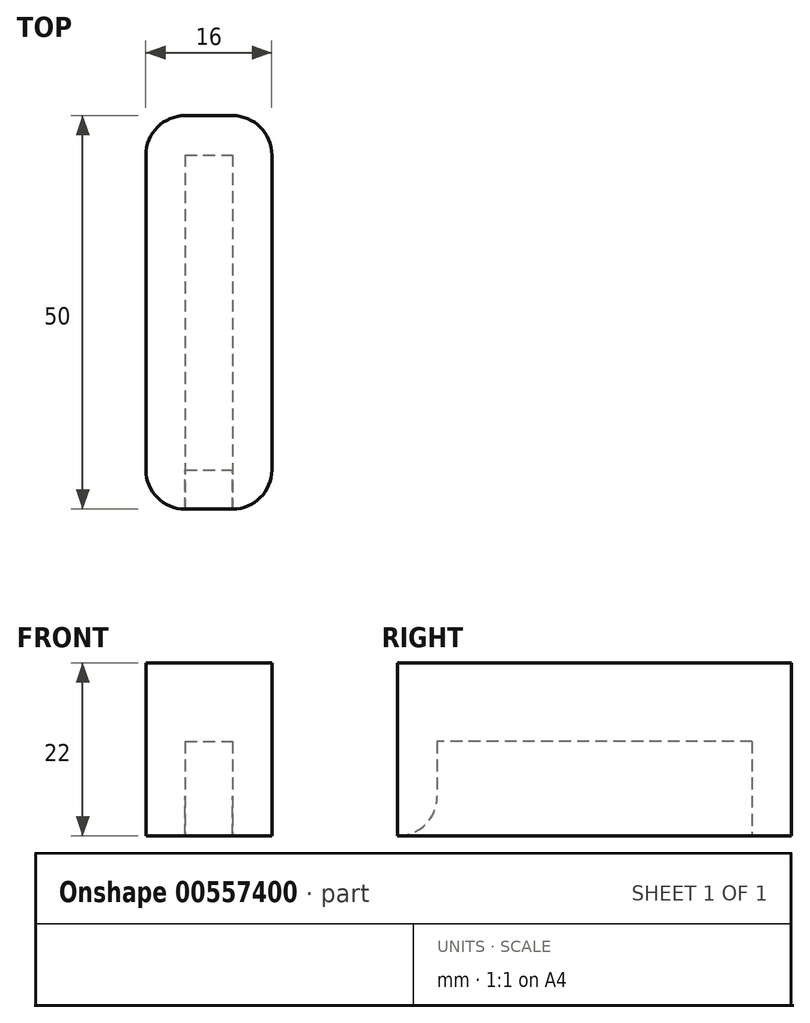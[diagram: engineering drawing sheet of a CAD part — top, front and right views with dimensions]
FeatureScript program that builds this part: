
annotation { "Feature Type Name" : "Feature", "Feature Type Description" : "" }
export const myFeature = defineFeature(function(context is Context, id is Id, definition is map)
    precondition{}
    {
        {
            var Q0;
            Q0=qCreatedBy(makeId("Top.planeOp"),FACE);
            var sketch = newSketch(context, id + "F0", { "sketchPlane" : qUnion([Q0])});
            skLineSegment(sketch, "E0.bottom", {"start": v(-26.05, 14.24) * mm, "end": v(-20.05, 14.24) * mm});
            skLineSegment(sketch, "E0.top", {"start": v(-26.05, -25.76) * mm, "end": v(-20.05, -25.76) * mm});
            skLineSegment(sketch, "E0.left", {"start": v(-26.05, 14.24) * mm, "end": v(-26.05, -25.76) * mm});
            skLineSegment(sketch, "E0.right", {"start": v(-20.05, 14.24) * mm, "end": v(-20.05, -25.76) * mm});
            skLineSegment(sketch, "E1.bottom", {"start": v(-15.05, -30.76) * mm, "end": v(-31.05, -30.76) * mm});
            skLineSegment(sketch, "E1.top", {"start": v(-15.05, 19.24) * mm, "end": v(-31.05, 19.24) * mm});
            skLineSegment(sketch, "E1.left", {"start": v(-15.05, -30.76) * mm, "end": v(-15.05, 19.24) * mm});
            skLineSegment(sketch, "E1.right", {"start": v(-31.05, -30.76) * mm, "end": v(-31.05, 19.24) * mm});
            skSolve(sketch);
        }
        {
            var Q0;
            Q0 = qSketchRegion(id + "F0", true);
            extrude(context, id + "F1", {"entities" : qUnion([Q0]), "depth" : 12 * mm, "offsetDistance" : 25 * mm});
        }
        {
            var Q0;
            Q0=makeQuery(id+"F1.opExtrude","CAP_FACE",FACE,{"disambiguationData":[OSD([sQuery(id+"F0.wireOp",EDGE,"E0.bottom"),sQuery(id+"F0.wireOp",EDGE,"E0.top"),sQuery(id+"F0.wireOp",EDGE,"E0.left"),sQuery(id+"F0.wireOp",EDGE,"E0.right"),sQuery(id+"F0.wireOp",EDGE,"E1.bottom"),sQuery(id+"F0.wireOp",EDGE,"E1.top"),sQuery(id+"F0.wireOp",EDGE,"E1.left"),sQuery(id+"F0.wireOp",EDGE,"E1.right")])],"isStart":false});
            var sketch = newSketch(context, id + "F2", { "sketchPlane" : qUnion([Q0])});
            skLineSegment(sketch, "E2.bottom", {"start": v(-31.05, 19.24) * mm, "end": v(-15.05, 19.24) * mm});
            skLineSegment(sketch, "E2.top", {"start": v(-31.05, -30.76) * mm, "end": v(-15.05, -30.76) * mm});
            skLineSegment(sketch, "E2.left", {"start": v(-31.05, 19.24) * mm, "end": v(-31.05, -30.76) * mm});
            skLineSegment(sketch, "E2.right", {"start": v(-15.05, 19.24) * mm, "end": v(-15.05, -30.76) * mm});
            skSolve(sketch);
        }
        {
            var Q0;
            Q0 = qSketchRegion(id + "F2", true);
            extrude(context, id + "F3", {"entities" : qUnion([Q0]), "operationType" : NewBodyOperationType.ADD, "depth" : 10 * mm, "offsetDistance" : 25 * mm});
        }
        {
            var Q0;
            Q0=makeQuery(id+"F1.opExtrude","CAP_EDGE",EDGE,{"disambiguationData":[OSD([sQuery(id+"F0.wireOp",EDGE,"E0.top")])],"isStart":true});
            fillet(context, id + "F4", {"entities" : qUnion([Q0]), "radius" : 5 * mm, "tangentPropagation" : true, "allowEdgeOverflow" : false});
        }
        {
            var Q0;
            Q0=makeQuery(id+"F3.boolean.opBoolean","MERGE",EDGE,{"derivedFrom":[makeQuery(id+"F1.opExtrude","SWEPT_EDGE",EDGE,{"disambiguationData":[OSD([sQuery(id+"F0.wireOp",EDGE,"E1.top"),sQuery(id+"F0.wireOp",EDGE,"E1.left")])]}),makeQuery(id+"F3.opExtrude","SWEPT_EDGE",EDGE,{"disambiguationData":[OSD([sQuery(id+"F2.wireOp",EDGE,"E2.bottom"),sQuery(id+"F2.wireOp",EDGE,"E2.right")])]})]});
            var Q1;
            Q1=makeQuery(id+"F3.boolean.opBoolean","MERGE",EDGE,{"derivedFrom":[makeQuery(id+"F1.opExtrude","SWEPT_EDGE",EDGE,{"disambiguationData":[OSD([sQuery(id+"F0.wireOp",EDGE,"E1.bottom"),sQuery(id+"F0.wireOp",EDGE,"E1.left")])]}),makeQuery(id+"F3.opExtrude","SWEPT_EDGE",EDGE,{"disambiguationData":[OSD([sQuery(id+"F2.wireOp",EDGE,"E2.top"),sQuery(id+"F2.wireOp",EDGE,"E2.right")])]})]});
            var Q2;
            Q2=makeQuery(id+"F3.boolean.opBoolean","MERGE",EDGE,{"derivedFrom":[makeQuery(id+"F1.opExtrude","SWEPT_EDGE",EDGE,{"disambiguationData":[OSD([sQuery(id+"F0.wireOp",EDGE,"E1.bottom"),sQuery(id+"F0.wireOp",EDGE,"E1.right")])]}),makeQuery(id+"F3.opExtrude","SWEPT_EDGE",EDGE,{"disambiguationData":[OSD([sQuery(id+"F2.wireOp",EDGE,"E2.top"),sQuery(id+"F2.wireOp",EDGE,"E2.left")])]})]});
            var Q3;
            Q3=makeQuery(id+"F3.boolean.opBoolean","MERGE",EDGE,{"derivedFrom":[makeQuery(id+"F1.opExtrude","SWEPT_EDGE",EDGE,{"disambiguationData":[OSD([sQuery(id+"F0.wireOp",EDGE,"E1.top"),sQuery(id+"F0.wireOp",EDGE,"E1.right")])]}),makeQuery(id+"F3.opExtrude","SWEPT_EDGE",EDGE,{"disambiguationData":[OSD([sQuery(id+"F2.wireOp",EDGE,"E2.bottom"),sQuery(id+"F2.wireOp",EDGE,"E2.left")])]})]});
            fillet(context, id + "F5", {"entities" : qUnion([Q0, Q1, Q2, Q3]), "radius" : 5 * mm, "tangentPropagation" : true, "allowEdgeOverflow" : false});
        }
    });
